# Revit family: ADB Armoire Foyer Electrique 400 IX2
name_source: partatom
category: Equipement spécialisé
units: mm (PartAtom-declared; Revit-internal decimal feet)

## family parameters
Basée sur le plan de construction = Non
Conserver l'orientation des annotations = Non
Cote de connecteur circulaire = Utiliser le diamètre
Couper avec des vides une fois chargée = Non
Numéro OmniClass = 23.40.40.14.17.11
Partagée = Non
Repère de localisation dans la pièce = Non
Titre OmniClass = Cookers, Ovens, Stoves
Toujours verticalement = Oui
Type d'élément = Normal

## types (2) — shared parameters
C = 140 mm  [stored 0.459318 ft]
Commentaires du type = Gamme Ambassade - Armoires - Foyers électriques
D = 765 mm  [stored 2.50984 ft]
Fabricant = Société Industrielle de Lacanche
URL = https://www.ambassade-de-bourgogne.com
URL catalogue = https://www.ambassade-de-bourgogne.com
zero-valued in all types: Elévation par défaut

## per-type parameters (varying)
| type | 410 IX | 423 IX | Description | Table |
| CME 410 IX | Oui | Non | Table électrique vitrocéramique 1 foyer induction | 1-2 foyers induction : 1 foyer |
| CME 423 IX | Non | Oui | Table électrique vitrocéramique 2 foyers induction | 1-2 foyers induction : 2 foyers |

note: column(s) folded — value = type name in every type: Modèle

note: [stored X ft] marks values corroborated as IEEE doubles in the binary element streams (Revit-internal decimal feet)
